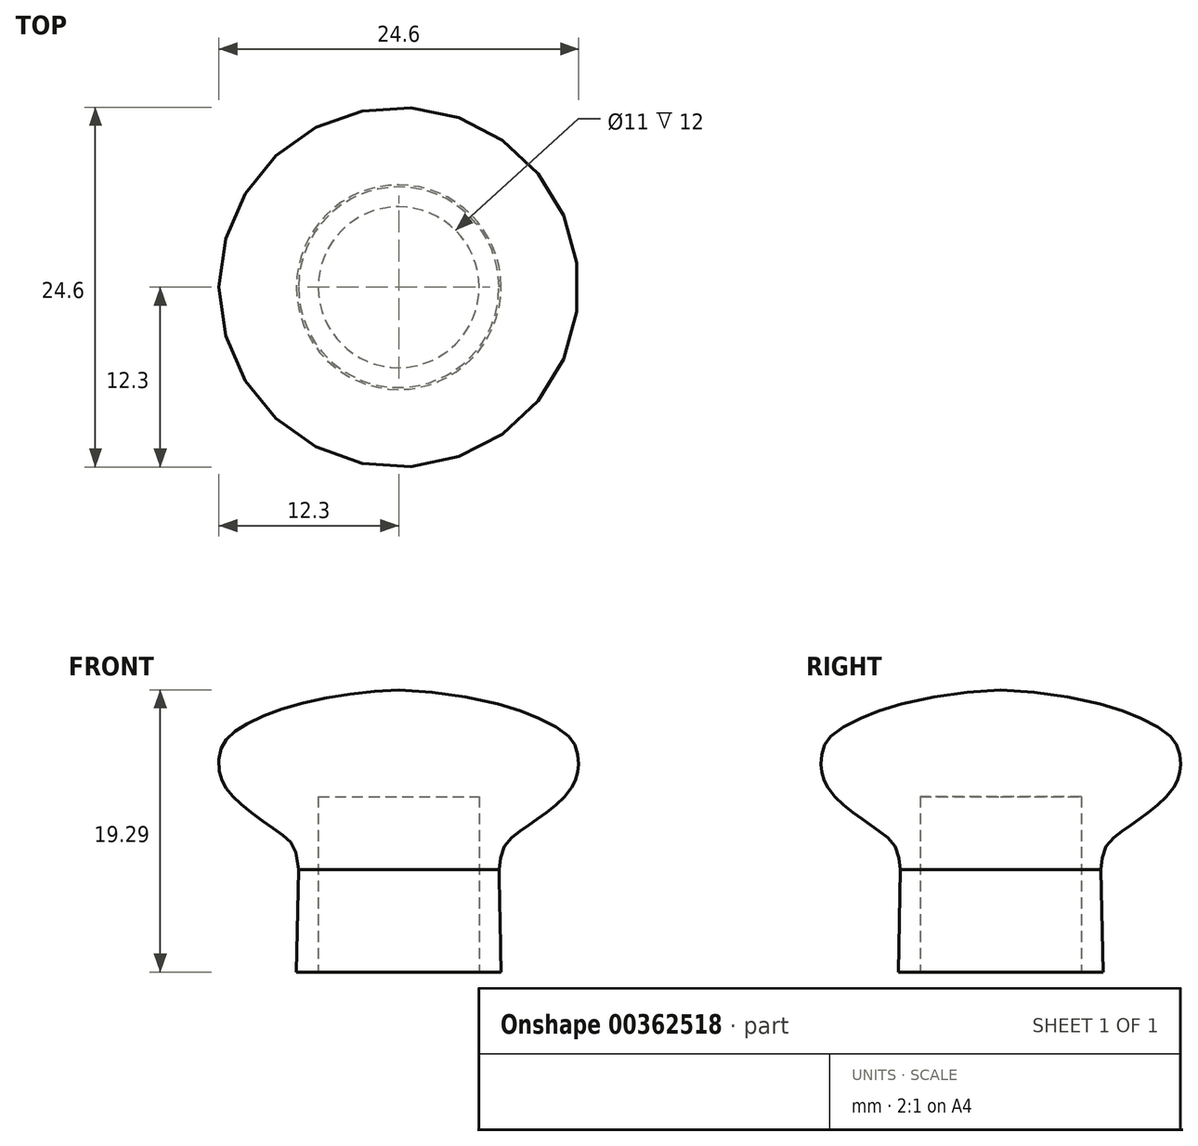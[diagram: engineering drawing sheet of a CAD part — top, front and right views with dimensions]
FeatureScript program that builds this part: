
annotation { "Feature Type Name" : "Feature", "Feature Type Description" : "" }
export const myFeature = defineFeature(function(context is Context, id is Id, definition is map)
    precondition{}
    {
        {
            var Q0;
            Q0=qCreatedBy(makeId("Front.planeOp"),FACE);
            var sketch = newSketch(context, id + "F0", { "sketchPlane" : qUnion([Q0])});
            skLineSegment(sketch, "E0", {"start": v(0, 0) * mm, "end": v(-7, 0) * mm});
            skLineSegment(sketch, "E1", {"start": v(-7, 0) * mm, "end": v(-6.86, 7) * mm});
            skFitSpline(sketch, "E2", {"points": [v(-6.86, 7) * mm, v(-7.62, 9.1) * mm, v(-9.11, 10.2) * mm, v(-10.94, 11.6) * mm, v(-11.86, 12.67) * mm, v(-12.25, 13.7) * mm, v(-12.14, 15.3) * mm, v(-11.13, 16.51) * mm, v(-7.22, 18.22) * mm, v(0, 19.29) * mm], "startDerivative": vector(-2.55, 35.73) * mm, "endDerivative": vector(37.1, 0.95) * mm});
            skLineSegment(sketch, "E3", {"start": v(0, 19.29) * mm, "end": v(0, 0) * mm});
            skSolve(sketch);
        }
        {
            var Q0;
            Q0 = qSketchRegion(id + "F0", true);
            var Q1;
            Q1=sQuery(id+"F0.wireOp",EDGE,"E3");
            revolve(context, id + "F1", {"entities" : qUnion([Q0]), "axis" : qUnion([Q1]), "revolveType" : RevolveType.FULL});
        }
        {
            var Q0;
            Q0=makeQuery(id+"F1.opRevolve","SWEPT_FACE",FACE,{"disambiguationData":[OSD([sQuery(id+"F0.wireOp",EDGE,"E0")])]});
            var sketch = newSketch(context, id + "F2", { "sketchPlane" : qUnion([Q0])});
            skCircle(sketch, "E4", {"center": v(0, 0) * mm, "radius": 5.5 * mm});
            skSolve(sketch);
        }
        {
            var Q0;
            Q0 = qSketchRegion(id + "F2", true);
            extrude(context, id + "F3", {"entities" : qUnion([Q0]), "operationType" : NewBodyOperationType.REMOVE, "oppositeDirection" : true, "depth" : 12 * mm, "offsetDistance" : 25 * mm});
        }
    });
